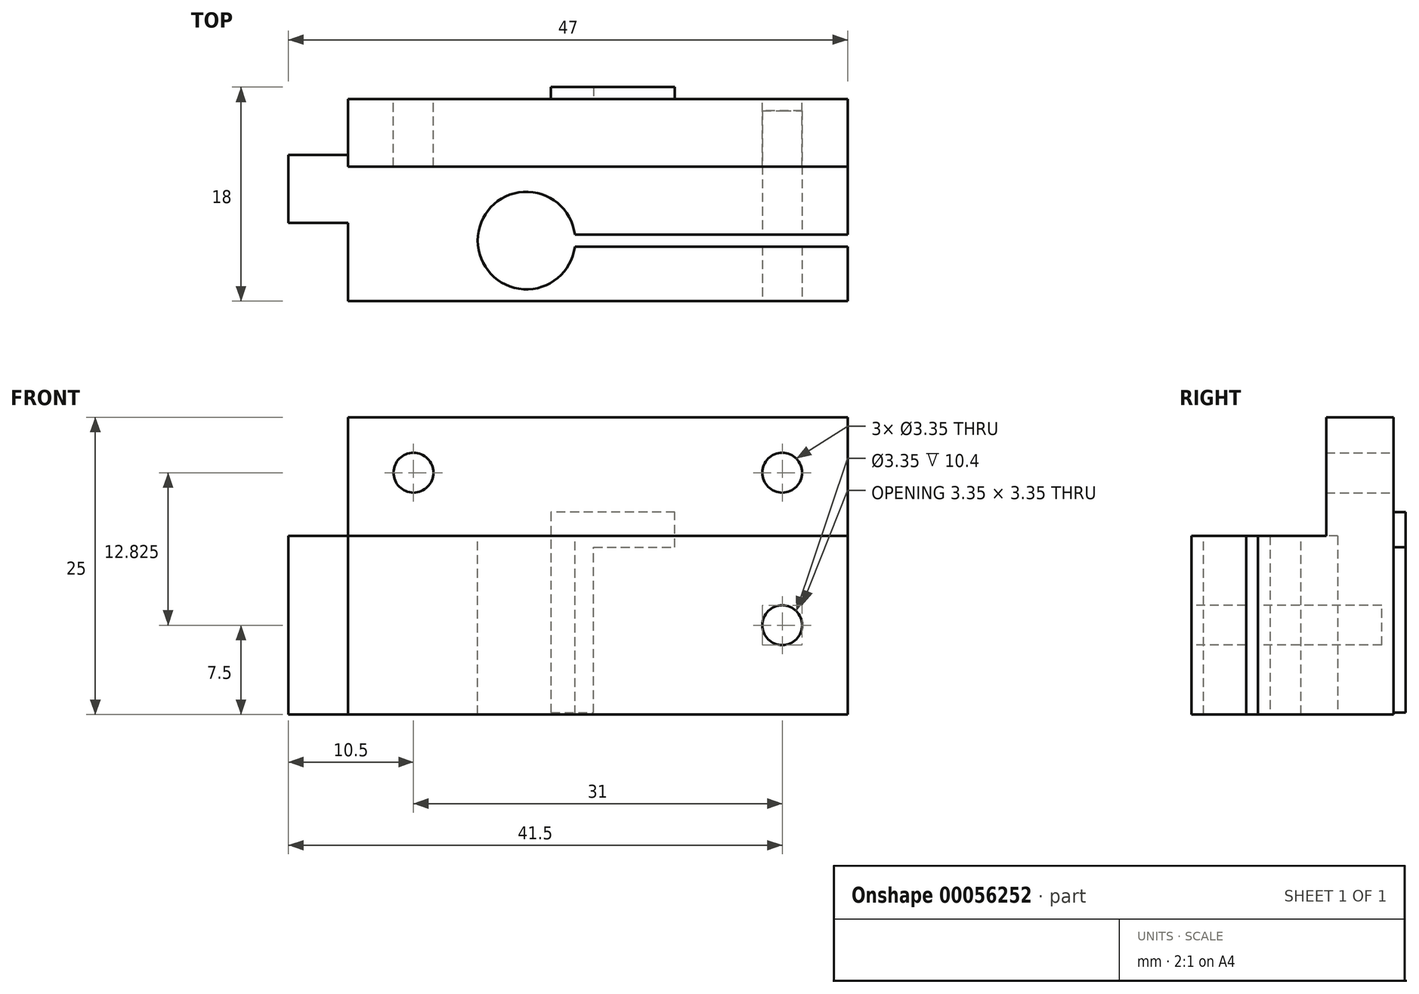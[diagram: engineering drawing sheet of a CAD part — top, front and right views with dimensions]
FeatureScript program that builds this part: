
annotation { "Feature Type Name" : "Feature", "Feature Type Description" : "" }
export const myFeature = defineFeature(function(context is Context, id is Id, definition is map)
    precondition{}
    {
        {
            var Q0;
            Q0=qCreatedBy(makeId("Top.planeOp"),FACE);
            var sketch = newSketch(context, id + "F0", { "sketchPlane" : qUnion([Q0])});
            skLineSegment(sketch, "E0.bottom", {"start": v(0, 0) * mm, "end": v(42, 0) * mm});
            skLineSegment(sketch, "E0.top", {"start": v(0, 17) * mm, "end": v(42, 17) * mm});
            skLineSegment(sketch, "E0.left", {"start": v(0, 0) * mm, "end": v(0, 17) * mm});
            skLineSegment(sketch, "E0.right", {"start": v(42, 0) * mm, "end": v(42, 17) * mm});
            skSolve(sketch);
        }
        {
            var Q0;
            Q0=qSketchRegion(id+"F0",true);
            extrude(context, id + "F1", {"entities" : qUnion([Q0]), "depth" : 15 * mm, "offsetDistance" : 25 * mm});
        }
        {
            var Q0;
            Q0=makeQuery(id+"F1.opExtrude","CAP_FACE",FACE,{"disambiguationData":[OSD([sQuery(id+"F0.wireOp",EDGE,"E0.bottom"),sQuery(id+"F0.wireOp",EDGE,"E0.top"),sQuery(id+"F0.wireOp",EDGE,"E0.left"),sQuery(id+"F0.wireOp",EDGE,"E0.right")])],"isStart":false});
            var sketch = newSketch(context, id + "F2", { "sketchPlane" : qUnion([Q0])});
            skCircle(sketch, "E1", {"center": v(15, 5.1) * mm, "radius": 4.1 * mm});
            skLineSegment(sketch, "E2", {"start": v(15, 5.1) * mm, "end": v(42, 5.1) * mm});
            skLineSegment(sketch, "E3", {"start": v(42, 5.1) * mm, "end": v(42, 4.6) * mm});
            skLineSegment(sketch, "E4", {"start": v(42, 4.6) * mm, "end": v(19.07, 4.6) * mm});
            skLineSegment(sketch, "E5", {"start": v(42, 5.1) * mm, "end": v(42, 5.6) * mm});
            skLineSegment(sketch, "E6", {"start": v(42, 5.6) * mm, "end": v(19.07, 5.6) * mm});
            skSolve(sketch);
        }
        {
            var Q0;
            Q0=makeQuery(id+"F1.opExtrude","SWEPT_FACE",FACE,{"disambiguationData":[OSD([sQuery(id+"F0.wireOp",EDGE,"E0.bottom")])]});
            var sketch = newSketch(context, id + "F3", { "sketchPlane" : qUnion([Q0])});
            skCircle(sketch, "E7", {"center": v(36.5, 7.5) * mm, "radius": 1.68 * mm});
            skPoint(sketch, "E8", {"position": v(42, 7.5) * mm});
            skSolve(sketch);
        }
        {
            var Q0;
            Q0=qSketchRegion(id+"F3",true);
            extrude(context, id + "F4", {"entities" : qUnion([Q0]), "operationType" : NewBodyOperationType.REMOVE, "oppositeDirection" : true, "depth" : 16 * mm, "offsetDistance" : 25 * mm});
        }
        {
            var Q0;
            Q0=makeQuery(id+"F1.opExtrude","CAP_FACE",FACE,{"disambiguationData":[OSD([sQuery(id+"F0.wireOp",EDGE,"E0.bottom"),sQuery(id+"F0.wireOp",EDGE,"E0.top"),sQuery(id+"F0.wireOp",EDGE,"E0.left"),sQuery(id+"F0.wireOp",EDGE,"E0.right")])],"isStart":false});
            var sketch = newSketch(context, id + "F5", { "sketchPlane" : qUnion([Q0])});
            skLineSegment(sketch, "E9.bottom", {"start": v(0, 17) * mm, "end": v(42, 17) * mm});
            skLineSegment(sketch, "E9.top", {"start": v(0, 11.33) * mm, "end": v(42, 11.33) * mm});
            skLineSegment(sketch, "E9.left", {"start": v(0, 17) * mm, "end": v(0, 11.33) * mm});
            skLineSegment(sketch, "E9.right", {"start": v(42, 17) * mm, "end": v(42, 11.33) * mm});
            skSolve(sketch);
        }
        {
            var Q0;
            Q0=makeQuery(id+"F5.imprint","IMPRINT",FACE,{"disambiguationData":[TD([[makeQuery(id+"F5.imprint","IMPRINT",EDGE,{"derivedFrom":sQuery(id+"F5.wireOp",EDGE,"E9.bottom")}),-1.0]])]});
            extrude(context, id + "F6", {"entities" : qUnion([Q0]), "operationType" : NewBodyOperationType.ADD, "depth" : 10 * mm});
        }
        {
            var Q0;
            Q0=makeQuery(id+"F6.boolean.opBoolean","MERGE",FACE,{"derivedFrom":[makeQuery(id+"F1.opExtrude","SWEPT_FACE",FACE,{"disambiguationData":[OSD([sQuery(id+"F0.wireOp",EDGE,"E0.top")])]}),makeQuery(id+"F6.opExtrude","SWEPT_FACE",FACE,{"disambiguationData":[OSD([sQuery(id+"FFFDCbTcivKPk1C_1.wireOp",EDGE,"d29ae964-e38a-46b3-8ff4-cadffaec6662.bottom")])]})]});
            var sketch = newSketch(context, id + "F7", { "sketchPlane" : qUnion([Q0])});
            skPoint(sketch, "E10", {"position": v(-36.5, 11.5) * mm});
            skCircle(sketch, "E11", {"center": v(-36.5, 20.33) * mm, "radius": 1.68 * mm});
            skCircle(sketch, "E12", {"center": v(-5.5, 20.33) * mm, "radius": 1.68 * mm});
            skSolve(sketch);
        }
        {
            var Q0;
            Q0=qSketchRegion(id+"F7",true);
            extrude(context, id + "F8", {"entities" : qUnion([Q0]), "operationType" : NewBodyOperationType.REMOVE, "oppositeDirection" : true, "depth" : 25 * mm});
        }
        {
            var Q0;
            Q0=qSketchRegion(id+"F2",true);
            extrude(context, id + "F9", {"entities" : qUnion([Q0]), "operationType" : NewBodyOperationType.REMOVE, "oppositeDirection" : true, "depth" : 25 * mm});
        }
        {
            var Q0;
            Q0=makeQuery(id+"F6.boolean.opBoolean","MERGE",FACE,{"derivedFrom":[makeQuery(id+"F1.opExtrude","SWEPT_FACE",FACE,{"disambiguationData":[OSD([sQuery(id+"F0.wireOp",EDGE,"E0.top")])]}),makeQuery(id+"F6.opExtrude","SWEPT_FACE",FACE,{"disambiguationData":[OSD([sQuery(id+"F5.wireOp",EDGE,"E9.bottom")])]})]});
            var sketch = newSketch(context, id + "F10", { "sketchPlane" : qUnion([Q0])});
            skText(sketch, "E13", { "text": "L", "fontName": "OpenSans-Bold.ttf"});
            const initialGuessF10  = {"E13": [-0.01494, 0.017, -1, 0, 0.017]};
            skSetInitialGuess(sketch, initialGuessF10);
            skSolve(sketch);
        }
        {
            var Q0;
            Q0=qSketchRegion(id+"F10",true);
            extrude(context, id + "F11", {"entities" : qUnion([Q0]), "operationType" : NewBodyOperationType.ADD, "depth" : 1 * mm});
        }
        {
            var Q0;
            Q0=makeQuery(id+"F6.boolean.opBoolean","MERGE",FACE,{"derivedFrom":[makeQuery(id+"F1.opExtrude","SWEPT_FACE",FACE,{"disambiguationData":[OSD([sQuery(id+"F0.wireOp",EDGE,"E0.left")])]}),makeQuery(id+"F6.opExtrude","SWEPT_FACE",FACE,{"disambiguationData":[OSD([sQuery(id+"F5.wireOp",EDGE,"E9.left")])]})]});
            var sketch = newSketch(context, id + "F12", { "sketchPlane" : qUnion([Q0])});
            skLineSegment(sketch, "E14.bottom", {"start": v(-12.3, 15) * mm, "end": v(-6.6, 15) * mm});
            skLineSegment(sketch, "E14.top", {"start": v(-12.3, 0) * mm, "end": v(-6.6, 0) * mm});
            skLineSegment(sketch, "E14.left", {"start": v(-12.3, 15) * mm, "end": v(-12.3, 0) * mm});
            skLineSegment(sketch, "E14.right", {"start": v(-6.6, 15) * mm, "end": v(-6.6, 0) * mm});
            skSolve(sketch);
        }
        {
            var Q0;
            Q0=qSketchRegion(id+"F12",true);
            extrude(context, id + "F13", {"entities" : qUnion([Q0]), "operationType" : NewBodyOperationType.ADD, "depth" : 5 * mm});
        }
    });
